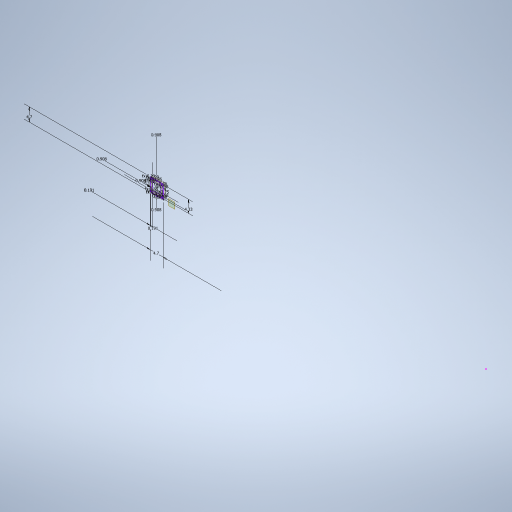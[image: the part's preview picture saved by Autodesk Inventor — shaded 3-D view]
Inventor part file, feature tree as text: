
AUTODESK INVENTOR PART (.ipt)
format: ipt  version: 2024 (Build 280153000, 153)  size: 364,544 bytes
history: native  units: in
note: dims shown in document units (in); Inventor stores cm internally (conversion verified against a paired STEP export)
features: extrude x4, fillet x3, plane x1, sketch x1
ambient origin geometry x8: Origin, YZ Plane, XZ Plane, XY Plane, X Axis, Y Axis, Z Axis, Center Point
bodies: Body1 (feature_tree)
feature tree (9):
  plane  "Work Plane3"
  sketch  "Sketch1"  dims[d1=1.8504in d2=1.8504in d4=0.0787in d6=0.0752in d7=0.0752in d8=1.7047in d9=1.7047in d10=0.0787in d14=0.0787in d17=0.0787in d24=0.3574in d25=0.3574in d26=0.3574in d27=0.3574in d32=0.315in d33=0.0in d45=0.3937in d46=0.0in d47=0.1181in d48=0.0in d51=0.0394in d52=0.0in d55=0.3937in d56=0.0787in d61=0.2283in d62=0.2283in d63=0.2283in d64=0.2283in d65=0.2283in d66=0.2283in d67=0.2283in d68=0.2283in d69=1.4764in d70=1.4764in d71=1.4764in d72=1.4764in d73=0.1142in d74=0.1142in d75=0.1575in]
  extrude  "Extrusion3"  Depth=1.8504in
  extrude  "Extrusion7"  Depth=0.0787in
  extrude  "Extrusion8"  Depth=0.0752in
  extrude  "Extrusion6"  Depth=0.0752in
  fillet  "Fillet5"  Radius=1.7047in
  fillet  "Fillet6"  Radius=1.7047in
  fillet  "Fillet7"  Radius=0.0787in
